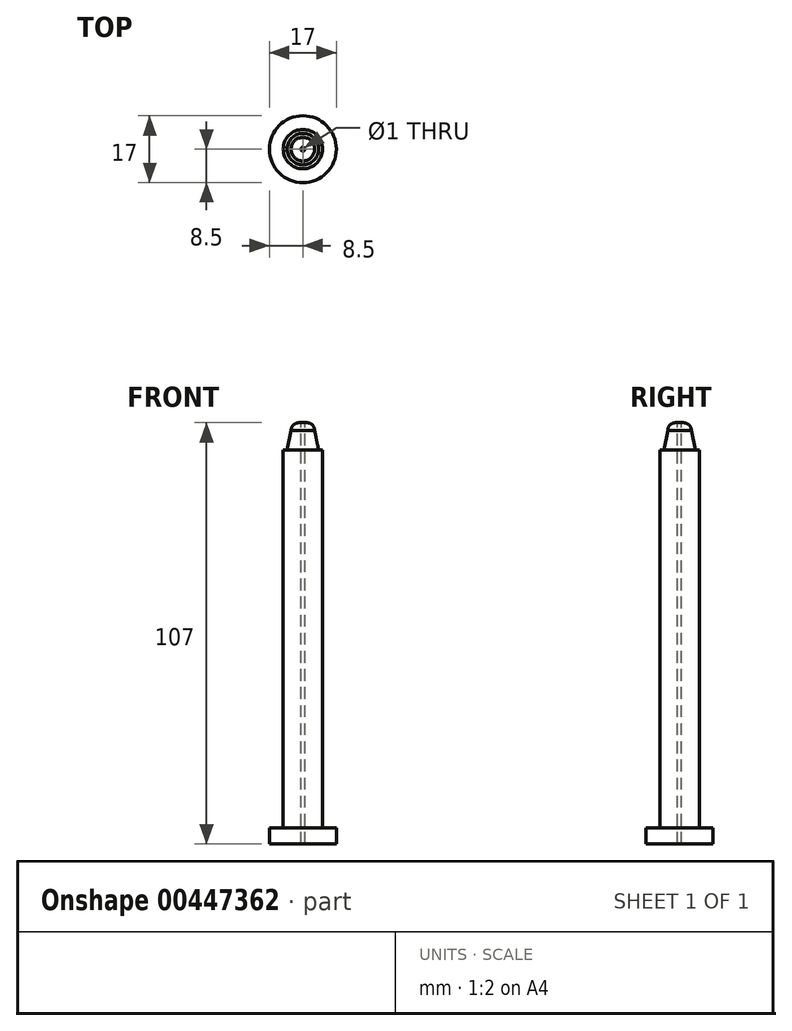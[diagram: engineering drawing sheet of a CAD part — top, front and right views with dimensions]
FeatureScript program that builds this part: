
annotation { "Feature Type Name" : "Feature", "Feature Type Description" : "" }
export const myFeature = defineFeature(function(context is Context, id is Id, definition is map)
    precondition{}
    {
        {
            var Q0;
            Q0=qCreatedBy(makeId("Top.planeOp"),FACE);
            var sketch = newSketch(context, id + "F0", { "sketchPlane" : qUnion([Q0])});
            skCircle(sketch, "E0", {"center": v(0, 0) * mm, "radius": 8.5 * mm});
            skSolve(sketch);
        }
        {
            var Q0;
            Q0=qSketchRegion(id+"F0",true);
            extrude(context, id + "F1", {"entities" : qUnion([Q0]), "depth" : 4 * mm});
        }
        {
            var Q0;
            Q0=qCreatedBy(makeId("Top.planeOp"),FACE);
            var sketch = newSketch(context, id + "F2", { "sketchPlane" : qUnion([Q0])});
            skCircle(sketch, "E1", {"center": v(0, 0) * mm, "radius": 5 * mm});
            skSolve(sketch);
        }
        {
            var Q0;
            Q0=qSketchRegion(id+"F2",true);
            extrude(context, id + "F3", {"entities" : qUnion([Q0]), "operationType" : NewBodyOperationType.ADD, "depth" : 100 * mm});
        }
        {
            var Q0;
            Q0=qCreatedBy(makeId("Right.planeOp"),FACE);
            var sketch = newSketch(context, id + "F4", { "sketchPlane" : qUnion([Q0])});
            skLineSegment(sketch, "E2", {"start": v(0, 105) * mm, "end": v(0, 100) * mm});
            skLineSegment(sketch, "E3", {"start": v(0, 100) * mm, "end": v(4, 100) * mm});
            skLineSegment(sketch, "E4", {"start": v(4, 100) * mm, "end": v(3, 105) * mm});
            skLineSegment(sketch, "E5", {"start": v(3, 105) * mm, "end": v(0, 105) * mm});
            skSolve(sketch);
        }
        {
            var Q0;
            Q0=makeQuery(id+"F4.imprint","IMPRINT",FACE,{"disambiguationData":[TD([[makeQuery(id+"F4.imprint","IMPRINT",EDGE,{"derivedFrom":sQuery(id+"F4.wireOp",EDGE,"E2")}),1.0]])]});
            var Q1;
            Q1=sQuery(id+"F4.wireOp",EDGE,"E2");
            revolve(context, id + "F5", {"operationType" : NewBodyOperationType.ADD, "entities" : qUnion([Q0]), "axis" : qUnion([Q1]), "revolveType" : RevolveType.FULL});
        }
        {
            var Q0;
            Q0=qCreatedBy(makeId("Right.planeOp"),FACE);
            var sketch = newSketch(context, id + "F6", { "sketchPlane" : qUnion([Q0])});
            skLineSegment(sketch, "E6", {"start": v(0, 107) * mm, "end": v(0, 105) * mm});
            skLineSegment(sketch, "E7", {"start": v(0, 105) * mm, "end": v(3, 105) * mm});
            skLineSegment(sketch, "E8", {"start": v(1, 107) * mm, "end": v(0, 107) * mm});
            skArc(sketch, "E9", {"start": v(3, 105) * mm, "mid": v(2.41, 106.41) * mm, "end": v(1, 107) * mm});
            skSolve(sketch);
        }
        {
            var Q0;
            Q0=makeQuery(id+"F6.imprint","IMPRINT",FACE,{"disambiguationData":[TD([[makeQuery(id+"F6.imprint","IMPRINT",EDGE,{"derivedFrom":sQuery(id+"F6.wireOp",EDGE,"E6")}),1.0]])]});
            var Q1;
            Q1=sQuery(id+"F6.wireOp",EDGE,"E6");
            revolve(context, id + "F7", {"operationType" : NewBodyOperationType.ADD, "entities" : qUnion([Q0]), "axis" : qUnion([Q1]), "revolveType" : RevolveType.FULL});
        }
        {
            var Q0;
            Q0=makeQuery(id+"F7.opRevolve","SWEPT_FACE",FACE,{"disambiguationData":[OSD([sQuery(id+"F6.wireOp",EDGE,"E8")])]});
            var sketch = newSketch(context, id + "F8", { "sketchPlane" : qUnion([Q0])});
            skCircle(sketch, "E10", {"center": v(0, 0) * mm, "radius": 0.5 * mm});
            skSolve(sketch);
        }
        {
            var Q0;
            Q0 = qSketchRegion(id + "F8", true);
            extrude(context, id + "F9", {"entities" : qUnion([Q0]), "operationType" : NewBodyOperationType.REMOVE, "oppositeDirection" : true, "depth" : 112.7 * mm});
        }
    });
